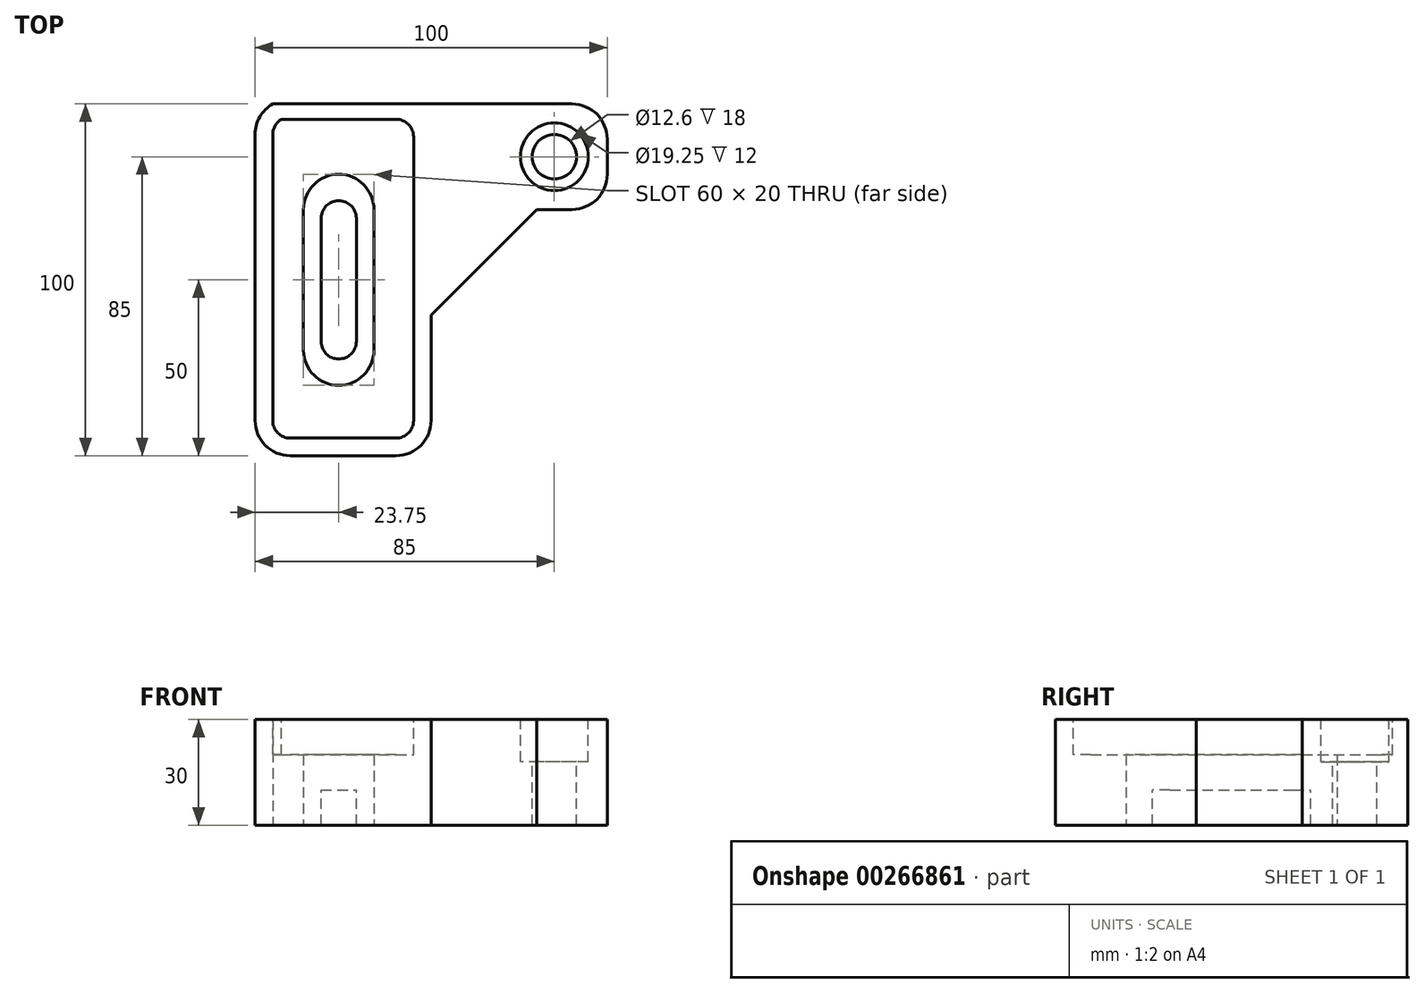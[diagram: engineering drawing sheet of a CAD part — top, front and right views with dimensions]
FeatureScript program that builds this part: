
annotation { "Feature Type Name" : "Feature", "Feature Type Description" : "" }
export const myFeature = defineFeature(function(context is Context, id is Id, definition is map)
    precondition{}
    {
        {
            var Q0;
            Q0=qCreatedBy(makeId("Top.planeOp"),FACE);
            var sketch = newSketch(context, id + "F0", { "sketchPlane" : qUnion([Q0])});
            skLineSegment(sketch, "E0", {"start": v(0, 0) * mm, "end": v(0, -30) * mm});
            skLineSegment(sketch, "E1", {"start": v(-10, -40) * mm, "end": v(-40, -40) * mm});
            skPoint(sketch, "E2.visualSharp", {"position": v(0, -40) * mm});
            skArc(sketch, "E2.filletArc", {"start": v(-10, -40) * mm, "mid": v(-2.93, -37.07) * mm, "end": v(0, -30) * mm});
            skLineSegment(sketch, "E3", {"start": v(-50, -30) * mm, "end": v(-50, 51.34) * mm});
            skPoint(sketch, "E4.visualSharp", {"position": v(-50, -40) * mm});
            skArc(sketch, "E4.filletArc", {"start": v(-50, -30) * mm, "mid": v(-47.07, -37.07) * mm, "end": v(-40, -40) * mm});
            skPoint(sketch, "E5.visualSharp", {"position": v(-50, 60) * mm});
            skArc(sketch, "E5.filletArc", {"start": v(-45, 60) * mm, "mid": v(-48.66, 56.34) * mm, "end": v(-50, 51.34) * mm});
            skLineSegment(sketch, "E6", {"start": v(0, 0) * mm, "end": v(30, 30) * mm});
            skLineSegment(sketch, "E7", {"start": v(30, 30) * mm, "end": v(40, 30) * mm});
            skLineSegment(sketch, "E8", {"start": v(50, 40) * mm, "end": v(50, 50) * mm});
            skLineSegment(sketch, "E9", {"start": v(-45, 60) * mm, "end": v(40, 60) * mm});
            skPoint(sketch, "E10.visualSharp", {"position": v(50, 30) * mm});
            skArc(sketch, "E10.filletArc", {"start": v(40, 30) * mm, "mid": v(47.07, 32.93) * mm, "end": v(50, 40) * mm});
            skPoint(sketch, "E11.visualSharp", {"position": v(50, 60) * mm});
            skArc(sketch, "E11.filletArc", {"start": v(50, 50) * mm, "mid": v(47.07, 57.07) * mm, "end": v(40, 60) * mm});
            skSolve(sketch);
        }
        {
            var Q0;
            Q0=makeQuery(id+"F0.imprint","IMPRINT",FACE,{"disambiguationData":[TD([[makeQuery(id+"F0.imprint","IMPRINT",EDGE,{"derivedFrom":sQuery(id+"F0.wireOp",EDGE,"E0")}),-1.0]])]});
            extrude(context, id + "F1", {"entities" : qUnion([Q0]), "depth" : 30 * mm});
        }
        {
            var Q0;
            Q0=makeQuery(id+"F1.opExtrude","CAP_FACE",FACE,{"disambiguationData":[OSD([sQuery(id+"F0.wireOp",EDGE,"E0"),sQuery(id+"F0.wireOp",EDGE,"E1"),sQuery(id+"F0.wireOp",EDGE,"E2.filletArc"),sQuery(id+"F0.wireOp",EDGE,"E3"),sQuery(id+"F0.wireOp",EDGE,"E4.filletArc"),sQuery(id+"F0.wireOp",EDGE,"E5.filletArc"),sQuery(id+"F0.wireOp",EDGE,"E6"),sQuery(id+"F0.wireOp",EDGE,"E7"),sQuery(id+"F0.wireOp",EDGE,"E8"),sQuery(id+"F0.wireOp",EDGE,"E9"),sQuery(id+"F0.wireOp",EDGE,"E10.filletArc"),sQuery(id+"F0.wireOp",EDGE,"E11.filletArc")])],"isStart":false});
            var sketch = newSketch(context, id + "F2", { "sketchPlane" : qUnion([Q0])});
            skPoint(sketch, "E12", {"position": v(35, 45) * mm});
            skSolve(sketch);
        }
        {
            var Q0;
            Q0=sQuery(id+"F2.wireOp",VERTEX,"E12");
            var Q1;
            Q1=makeQuery(id+"F1.opExtrude","SWEPT_BODY",BODY,{"disambiguationData":[OSD([sQuery(id+"F0.wireOp",EDGE,"E0"),sQuery(id+"F0.wireOp",EDGE,"E1"),sQuery(id+"F0.wireOp",EDGE,"E2.filletArc"),sQuery(id+"F0.wireOp",EDGE,"E3"),sQuery(id+"F0.wireOp",EDGE,"E4.filletArc"),sQuery(id+"F0.wireOp",EDGE,"E5.filletArc"),sQuery(id+"F0.wireOp",EDGE,"E6"),sQuery(id+"F0.wireOp",EDGE,"E7"),sQuery(id+"F0.wireOp",EDGE,"E8"),sQuery(id+"F0.wireOp",EDGE,"E9"),sQuery(id+"F0.wireOp",EDGE,"E10.filletArc"),sQuery(id+"F0.wireOp",EDGE,"E11.filletArc")])]});
            hole(context, id + "F3", {"style" : HoleStyle.C_BORE, "endStyle" : HoleEndStyle.THROUGH, "standardTappedOrClearance" : lookupTablePath({ "standard" : "ISO", "fit" : "Close", "size" : "M12", "type" : "Clearance" }), "standardBlindInLast" : lookupTablePath({ "fit" : "Close", "standard" : "ISO", "size" : "M12", "type" : "Clearance" }), "holeDiameter" : 12.6 * mm, "cBoreDiameter" : 19.25 * mm, "cBoreDepth" : 12 * mm, "tappedDepth" : 12 * mm, "tapClearance" : 3, "locations" : qUnion([Q0]), "scope" : qUnion([Q1])});
        }
        {
            var Q0;
            Q0=makeQuery(id+"F1.opExtrude","CAP_FACE",FACE,{"disambiguationData":[OSD([sQuery(id+"F0.wireOp",EDGE,"E0"),sQuery(id+"F0.wireOp",EDGE,"E1"),sQuery(id+"F0.wireOp",EDGE,"E2.filletArc"),sQuery(id+"F0.wireOp",EDGE,"E3"),sQuery(id+"F0.wireOp",EDGE,"E4.filletArc"),sQuery(id+"F0.wireOp",EDGE,"E5.filletArc"),sQuery(id+"F0.wireOp",EDGE,"E6"),sQuery(id+"F0.wireOp",EDGE,"E7"),sQuery(id+"F0.wireOp",EDGE,"E8"),sQuery(id+"F0.wireOp",EDGE,"E9"),sQuery(id+"F0.wireOp",EDGE,"E10.filletArc"),sQuery(id+"F0.wireOp",EDGE,"E11.filletArc")])],"isStart":false});
            var sketch = newSketch(context, id + "F4", { "sketchPlane" : qUnion([Q0])});
            skArc(sketch, "E13.0", {"start": v(-42.5, 55.67) * mm, "mid": v(-44.33, 53.84) * mm, "end": v(-45, 51.34) * mm});
            skLineSegment(sketch, "E13.1", {"start": v(-45, -30) * mm, "end": v(-45, 51.34) * mm});
            skArc(sketch, "E13.3", {"start": v(-10, -35) * mm, "mid": v(-6.46, -33.54) * mm, "end": v(-5, -30) * mm});
            skLineSegment(sketch, "E13.4", {"start": v(-10, -35) * mm, "end": v(-40, -35) * mm});
            skArc(sketch, "E13.5", {"start": v(-45, -30) * mm, "mid": v(-43.54, -33.54) * mm, "end": v(-40, -35) * mm});
            skLineSegment(sketch, "E14", {"start": v(-42.5, 55.67) * mm, "end": v(-10, 55.67) * mm});
            skLineSegment(sketch, "E15", {"start": v(-5, -30) * mm, "end": v(-5, 50.67) * mm});
            skArc(sketch, "E16.filletArc", {"start": v(-5, 50.67) * mm, "mid": v(-6.46, 54.2) * mm, "end": v(-10, 55.67) * mm});
            skLineSegment(sketch, "E17", {"start": v(-50, 10.67) * mm, "end": v(-5, 10.67) * mm, "construction": true});
            skLineSegment(sketch, "E18", {"start": v(-26.25, 55.67) * mm, "end": v(-26.25, 10.67) * mm, "construction": true});
            skSolve(sketch);
        }
        {
            var Q0;
            Q0=makeQuery(id+"F4.imprint","IMPRINT",FACE,{"disambiguationData":[TD([[makeQuery(id+"F4.imprint","IMPRINT",EDGE,{"derivedFrom":sQuery(id+"F4.wireOp",EDGE,"E13.0")}),1.0]])]});
            extrude(context, id + "F5", {"entities" : qUnion([Q0]), "operationType" : NewBodyOperationType.REMOVE, "oppositeDirection" : true, "depth" : 20 * mm});
        }
        {
            var Q0;
            Q0=makeQuery(id+"F5.boolean.opBoolean","COPY",FACE,{"derivedFrom":makeQuery(id+"F5.opExtrude","CAP_FACE",FACE,{"disambiguationData":[OSD([sQuery(id+"F4.wireOp",EDGE,"E13.0"),sQuery(id+"F4.wireOp",EDGE,"E13.1"),sQuery(id+"F4.wireOp",EDGE,"E13.3"),sQuery(id+"F4.wireOp",EDGE,"E13.4"),sQuery(id+"F4.wireOp",EDGE,"E13.5"),sQuery(id+"F4.wireOp",EDGE,"E14"),sQuery(id+"F4.wireOp",EDGE,"E15"),sQuery(id+"F4.wireOp",EDGE,"E16.filletArc")])],"isStart":false})});
            var sketch = newSketch(context, id + "F6", { "sketchPlane" : qUnion([Q0])});
            skLineSegment(sketch, "E19", {"start": v(-26.25, 30) * mm, "end": v(-26.25, -10) * mm, "construction": true});
            skPoint(sketch, "E19.startSnap0", {"position": v(-26.25, 55.67) * mm});
            skLineSegment(sketch, "E20.0", {"start": v(-45, -30) * mm, "end": v(-45, 51.34) * mm});
            skLineSegment(sketch, "E21.0", {"start": v(-42.5, 55.67) * mm, "end": v(-10, 55.67) * mm});
            skPoint(sketch, "E22", {"position": v(-26.25, 10) * mm});
            skArc(sketch, "E23.0.startCap", {"start": v(-36.25, 30) * mm, "mid": v(-26.25, 40) * mm, "end": v(-16.25, 30) * mm});
            skArc(sketch, "E23.0.endCap", {"start": v(-16.25, -10) * mm, "mid": v(-26.25, -20) * mm, "end": v(-36.25, -10) * mm});
            skLineSegment(sketch, "E23.0.left", {"start": v(-16.25, 30) * mm, "end": v(-16.25, -10) * mm});
            skLineSegment(sketch, "E23.0.right", {"start": v(-36.25, 30) * mm, "end": v(-36.25, -10) * mm});
            skSolve(sketch);
        }
        {
            var Q0;
            Q0=makeQuery(id+"F6.imprint","IMPRINT",FACE,{"disambiguationData":[TD([[makeQuery(id+"F6.imprint","IMPRINT",EDGE,{"derivedFrom":sQuery(id+"F6.wireOp",EDGE,"E23.0.startCap")}),-1.0]])]});
            extrude(context, id + "F7", {"entities" : qUnion([Q0]), "operationType" : NewBodyOperationType.ADD, "depth" : 10 * mm});
        }
        {
            var Q0;
            Q0=makeQuery(id+"F7.opExtrude","CAP_FACE",FACE,{"disambiguationData":[OSD([sQuery(id+"F6.wireOp",EDGE,"E23.0.startCap"),sQuery(id+"F6.wireOp",EDGE,"E23.0.endCap"),sQuery(id+"F6.wireOp",EDGE,"E23.0.left"),sQuery(id+"F6.wireOp",EDGE,"E23.0.right")])],"isStart":false});
            var sketch = newSketch(context, id + "F8", { "sketchPlane" : qUnion([Q0])});
            skLineSegment(sketch, "E24", {"start": v(-26.25, -7.5) * mm, "end": v(-26.25, 27.5) * mm, "construction": true});
            skArc(sketch, "E25.0.startCap", {"start": v(-21.25, -7.5) * mm, "mid": v(-26.25, -12.5) * mm, "end": v(-31.25, -7.5) * mm});
            skArc(sketch, "E25.0.endCap", {"start": v(-31.25, 27.5) * mm, "mid": v(-26.25, 32.5) * mm, "end": v(-21.25, 27.5) * mm});
            skLineSegment(sketch, "E25.0.left", {"start": v(-31.25, -7.5) * mm, "end": v(-31.25, 27.5) * mm});
            skLineSegment(sketch, "E25.0.right", {"start": v(-21.25, -7.5) * mm, "end": v(-21.25, 27.5) * mm});
            skSolve(sketch);
        }
        {
            var Q0;
            Q0=makeQuery(id+"F5.boolean.opBoolean","COPY",FACE,{"derivedFrom":makeQuery(id+"F5.opExtrude","CAP_FACE",FACE,{"disambiguationData":[OSD([sQuery(id+"F4.wireOp",EDGE,"E13.0"),sQuery(id+"F4.wireOp",EDGE,"E13.1"),sQuery(id+"F4.wireOp",EDGE,"E13.3"),sQuery(id+"F4.wireOp",EDGE,"E13.4"),sQuery(id+"F4.wireOp",EDGE,"E13.5"),sQuery(id+"F4.wireOp",EDGE,"E14"),sQuery(id+"F4.wireOp",EDGE,"E15"),sQuery(id+"F4.wireOp",EDGE,"E16.filletArc")])],"isStart":false})});
            fillet(context, id + "F9", {"entities" : qUnion([Q0]), "radius" : 2 * mm, "tangentPropagation" : true, "allowEdgeOverflow" : false});
        }
        {
            var Q0;
            Q0=makeQuery(id+"F8.imprint","IMPRINT",FACE,{"disambiguationData":[TD([[makeQuery(id+"F8.imprint","IMPRINT",EDGE,{"derivedFrom":sQuery(id+"F8.wireOp",EDGE,"E25.0.startCap")}),-1.0]])]});
            extrude(context, id + "F10", {"entities" : qUnion([Q0]), "operationType" : NewBodyOperationType.REMOVE, "endBound" : BoundingType.THROUGH_ALL, "oppositeDirection" : true, "depth" : 25 * mm});
        }
    });
